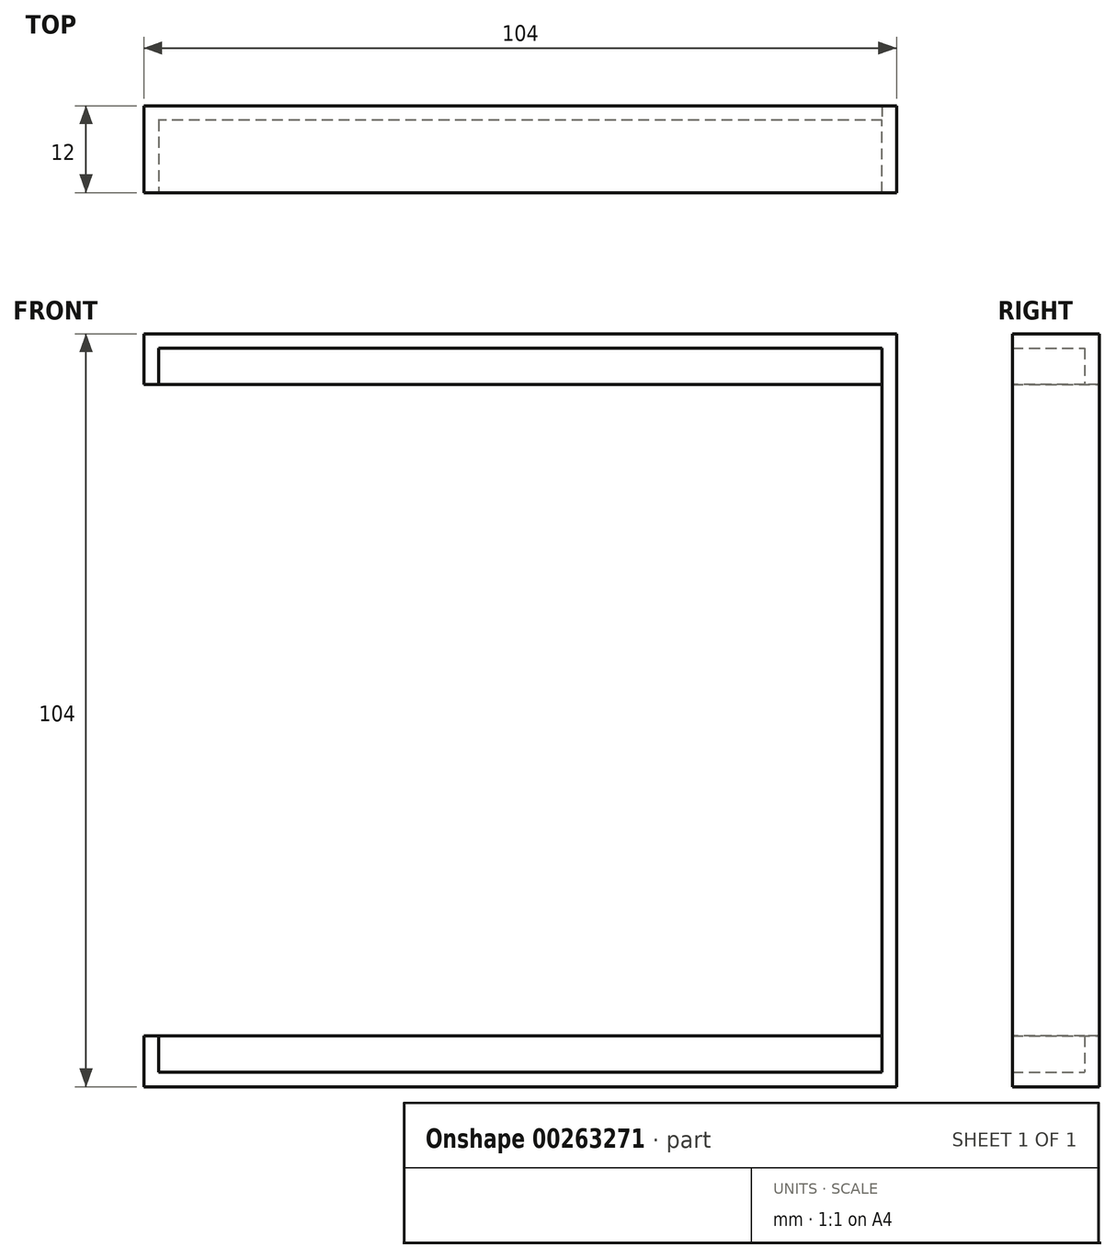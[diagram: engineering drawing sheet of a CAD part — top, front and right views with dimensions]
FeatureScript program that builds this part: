
annotation { "Feature Type Name" : "Feature", "Feature Type Description" : "" }
export const myFeature = defineFeature(function(context is Context, id is Id, definition is map)
    precondition{}
    {
        {
            var Q0;
            Q0=qCreatedBy(makeId("Front.planeOp"),FACE);
            var sketch = newSketch(context, id + "F0", { "sketchPlane" : qUnion([Q0])});
            skLineSegment(sketch, "E0.bottom", {"start": v(52, -52) * mm, "end": v(-52, -52) * mm});
            skLineSegment(sketch, "E0.top", {"start": v(52, 52) * mm, "end": v(-52, 52) * mm});
            skLineSegment(sketch, "E0.left", {"start": v(52, -52) * mm, "end": v(52, 52) * mm});
            skLineSegment(sketch, "E0.right", {"start": v(-52, -52) * mm, "end": v(-52, 52) * mm});
            skPoint(sketch, "E0.middle", {"position": v(0, 0) * mm});
            skSolve(sketch);
        }
        {
            var Q0;
            Q0 = qSketchRegion(id + "F0", true);
            extrude(context, id + "F1", {"entities" : qUnion([Q0]), "depth" : 2 * mm});
        }
        {
            var Q0;
            Q0=makeQuery(id+"F1.opExtrude","CAP_FACE",FACE,{"disambiguationData":[OSD([sQuery(id+"F0.wireOp",EDGE,"E0.bottom"),sQuery(id+"F0.wireOp",EDGE,"E0.top"),sQuery(id+"F0.wireOp",EDGE,"E0.left"),sQuery(id+"F0.wireOp",EDGE,"E0.right")])],"isStart":false});
            shell(context, id + "F2", {"entities" : qUnion([Q0]), "thickness" : 2 * mm});
        }
        {
            var Q0;
            Q0=makeQuery(id+"F1.opExtrude","CAP_FACE",FACE,{"disambiguationData":[OSD([sQuery(id+"F0.wireOp",EDGE,"E0.bottom"),sQuery(id+"F0.wireOp",EDGE,"E0.top"),sQuery(id+"F0.wireOp",EDGE,"E0.left"),sQuery(id+"F0.wireOp",EDGE,"E0.right")])],"isStart":false});
            var sketch = newSketch(context, id + "F3", { "sketchPlane" : qUnion([Q0])});
            skLineSegment(sketch, "E1.bottom", {"start": v(-52, 52) * mm, "end": v(52, 52) * mm});
            skLineSegment(sketch, "E1.top", {"start": v(-52, 50) * mm, "end": v(52, 50) * mm});
            skLineSegment(sketch, "E1.left", {"start": v(-52, 52) * mm, "end": v(-52, 50) * mm});
            skLineSegment(sketch, "E1.right", {"start": v(52, 52) * mm, "end": v(52, 50) * mm});
            skSolve(sketch);
        }
        {
            var Q0;
            Q0 = qSketchRegion(id + "F3", true);
            extrude(context, id + "F4", {"entities" : qUnion([Q0]), "operationType" : NewBodyOperationType.ADD, "depth" : 10 * mm});
        }
        {
            var Q0;
            Q0=makeQuery(id+"F1.opExtrude","CAP_FACE",FACE,{"disambiguationData":[OSD([sQuery(id+"F0.wireOp",EDGE,"E0.bottom"),sQuery(id+"F0.wireOp",EDGE,"E0.top"),sQuery(id+"F0.wireOp",EDGE,"E0.left"),sQuery(id+"F0.wireOp",EDGE,"E0.right")])],"isStart":false});
            var sketch = newSketch(context, id + "F5", { "sketchPlane" : qUnion([Q0])});
            skLineSegment(sketch, "E2.bottom", {"start": v(-52, -52) * mm, "end": v(52, -52) * mm});
            skLineSegment(sketch, "E2.top", {"start": v(-52, -50) * mm, "end": v(52, -50) * mm});
            skLineSegment(sketch, "E2.left", {"start": v(-52, -52) * mm, "end": v(-52, -50) * mm});
            skLineSegment(sketch, "E2.right", {"start": v(52, -52) * mm, "end": v(52, -50) * mm});
            skSolve(sketch);
        }
        {
            var Q0;
            Q0 = qSketchRegion(id + "F5", true);
            extrude(context, id + "F6", {"entities" : qUnion([Q0]), "operationType" : NewBodyOperationType.ADD, "depth" : 10 * mm});
        }
        {
            var Q0;
            Q0=makeQuery(id+"F1.opExtrude","CAP_FACE",FACE,{"disambiguationData":[OSD([sQuery(id+"F0.wireOp",EDGE,"E0.bottom"),sQuery(id+"F0.wireOp",EDGE,"E0.top"),sQuery(id+"F0.wireOp",EDGE,"E0.left"),sQuery(id+"F0.wireOp",EDGE,"E0.right")])],"isStart":false});
            var sketch = newSketch(context, id + "F7", { "sketchPlane" : qUnion([Q0])});
            skLineSegment(sketch, "E3.bottom", {"start": v(-52, 50) * mm, "end": v(-50, 50) * mm});
            skLineSegment(sketch, "E3.top", {"start": v(-52, -50) * mm, "end": v(-50, -50) * mm});
            skLineSegment(sketch, "E3.left", {"start": v(-52, 50) * mm, "end": v(-52, -50) * mm});
            skLineSegment(sketch, "E3.right", {"start": v(-50, 50) * mm, "end": v(-50, -50) * mm});
            skSolve(sketch);
        }
        {
            var Q0;
            Q0 = qSketchRegion(id + "F7", true);
            extrude(context, id + "F8", {"entities" : qUnion([Q0]), "operationType" : NewBodyOperationType.ADD, "depth" : 10 * mm});
        }
        {
            var Q0;
            Q0=makeQuery(id+"F1.opExtrude","CAP_FACE",FACE,{"disambiguationData":[OSD([sQuery(id+"F0.wireOp",EDGE,"E0.bottom"),sQuery(id+"F0.wireOp",EDGE,"E0.top"),sQuery(id+"F0.wireOp",EDGE,"E0.left"),sQuery(id+"F0.wireOp",EDGE,"E0.right")])],"isStart":false});
            var sketch = newSketch(context, id + "F9", { "sketchPlane" : qUnion([Q0])});
            skLineSegment(sketch, "E4.bottom", {"start": v(52, 50) * mm, "end": v(50, 50) * mm});
            skLineSegment(sketch, "E4.top", {"start": v(52, -50) * mm, "end": v(50, -50) * mm});
            skLineSegment(sketch, "E4.left", {"start": v(52, 50) * mm, "end": v(52, -50) * mm});
            skLineSegment(sketch, "E4.right", {"start": v(50, 50) * mm, "end": v(50, -50) * mm});
            skSolve(sketch);
        }
        {
            var Q0;
            Q0 = qSketchRegion(id + "F9", true);
            extrude(context, id + "F10", {"entities" : qUnion([Q0]), "operationType" : NewBodyOperationType.ADD, "depth" : 10 * mm});
        }
        {
            var Q0;
            Q0=makeQuery(id+"F1.opExtrude","CAP_FACE",FACE,{"disambiguationData":[OSD([sQuery(id+"F0.wireOp",EDGE,"E0.bottom"),sQuery(id+"F0.wireOp",EDGE,"E0.top"),sQuery(id+"F0.wireOp",EDGE,"E0.left"),sQuery(id+"F0.wireOp",EDGE,"E0.right")])],"isStart":false});
            var sketch = newSketch(context, id + "F11", { "sketchPlane" : qUnion([Q0])});
            skLineSegment(sketch, "E5.bottom", {"start": v(50, -50) * mm, "end": v(-50, -50) * mm});
            skLineSegment(sketch, "E5.top", {"start": v(50, -45) * mm, "end": v(-50, -45) * mm});
            skLineSegment(sketch, "E5.left", {"start": v(50, -50) * mm, "end": v(50, -45) * mm});
            skLineSegment(sketch, "E5.right", {"start": v(-50, -50) * mm, "end": v(-50, -45) * mm});
            skSolve(sketch);
        }
        {
            var Q0;
            Q0=makeQuery(id+"F1.opExtrude","CAP_FACE",FACE,{"disambiguationData":[OSD([sQuery(id+"F0.wireOp",EDGE,"E0.bottom"),sQuery(id+"F0.wireOp",EDGE,"E0.top"),sQuery(id+"F0.wireOp",EDGE,"E0.left"),sQuery(id+"F0.wireOp",EDGE,"E0.right")])],"isStart":false});
            var sketch = newSketch(context, id + "F12", { "sketchPlane" : qUnion([Q0])});
            skLineSegment(sketch, "E6.bottom", {"start": v(-50, 50) * mm, "end": v(50, 50) * mm});
            skLineSegment(sketch, "E6.top", {"start": v(-50, 45) * mm, "end": v(50, 45) * mm});
            skLineSegment(sketch, "E6.left", {"start": v(-50, 50) * mm, "end": v(-50, 45) * mm});
            skLineSegment(sketch, "E6.right", {"start": v(50, 50) * mm, "end": v(50, 45) * mm});
            skSolve(sketch);
        }
        {
            var Q0;
            Q0=makeQuery(id+"F1.opExtrude","CAP_FACE",FACE,{"disambiguationData":[OSD([sQuery(id+"F0.wireOp",EDGE,"E0.bottom"),sQuery(id+"F0.wireOp",EDGE,"E0.top"),sQuery(id+"F0.wireOp",EDGE,"E0.left"),sQuery(id+"F0.wireOp",EDGE,"E0.right")])],"isStart":false});
            var sketch = newSketch(context, id + "F13", { "sketchPlane" : qUnion([Q0])});
            skLineSegment(sketch, "E7.bottom", {"start": v(50, 45) * mm, "end": v(-61.43, 45) * mm});
            skLineSegment(sketch, "E7.top", {"start": v(50, -45) * mm, "end": v(-61.43, -45) * mm});
            skLineSegment(sketch, "E7.left", {"start": v(50, 45) * mm, "end": v(50, -45) * mm});
            skLineSegment(sketch, "E7.right", {"start": v(-61.43, 45) * mm, "end": v(-61.43, -45) * mm});
            skSolve(sketch);
        }
        {
            var Q0;
            Q0 = qSketchRegion(id + "F13", true);
            extrude(context, id + "F14", {"entities" : qUnion([Q0]), "operationType" : NewBodyOperationType.REMOVE, "oppositeDirection" : true, "depth" : 25 * mm});
        }
        {
            var Q0;
            Q0=makeQuery(id+"F8.boolean.opBoolean","MERGE",FACE,{"derivedFrom":[makeQuery(id+"F6.boolean.opBoolean","MERGE",FACE,{"derivedFrom":[makeQuery(id+"F4.boolean.opBoolean","MERGE",FACE,{"derivedFrom":[makeQuery(id+"F1.opExtrude","SWEPT_FACE",FACE,{"disambiguationData":[OSD([sQuery(id+"F0.wireOp",EDGE,"E0.right")])]}),makeQuery(id+"F4.opExtrude","SWEPT_FACE",FACE,{"disambiguationData":[OSD([sQuery(id+"F3.wireOp",EDGE,"E1.left")])]})]}),makeQuery(id+"F6.opExtrude","SWEPT_FACE",FACE,{"disambiguationData":[OSD([sQuery(id+"F5.wireOp",EDGE,"E2.left")])]})]}),makeQuery(id+"F8.opExtrude","SWEPT_FACE",FACE,{"disambiguationData":[OSD([sQuery(id+"F7.wireOp",EDGE,"E3.left")])]})]});
            var sketch = newSketch(context, id + "F15", { "sketchPlane" : qUnion([Q0])});
            skLineSegment(sketch, "E8.bottom", {"start": v(2, 45) * mm, "end": v(2, 45) * mm});
            skLineSegment(sketch, "E8.top", {"start": v(2, -45) * mm, "end": v(2, -45) * mm});
            skLineSegment(sketch, "E8.left", {"start": v(2, 45) * mm, "end": v(2, -45) * mm});
            skLineSegment(sketch, "E8.right", {"start": v(2, 45) * mm, "end": v(2, -45) * mm});
            skLineSegment(sketch, "E9.bottom", {"start": v(17.08, -45) * mm, "end": v(2, -45) * mm});
            skLineSegment(sketch, "E9.top", {"start": v(17.08, 45) * mm, "end": v(2, 45) * mm});
            skLineSegment(sketch, "E9.left", {"start": v(17.08, -45) * mm, "end": v(17.08, 45) * mm});
            skLineSegment(sketch, "E9.right", {"start": v(2, -45) * mm, "end": v(2, 45) * mm});
            skSolve(sketch);
        }
        {
            var Q0;
            Q0 = qSketchRegion(id + "F15", true);
            extrude(context, id + "F16", {"entities" : qUnion([Q0]), "operationType" : NewBodyOperationType.REMOVE, "oppositeDirection" : true, "depth" : 25 * mm});
        }
    });
